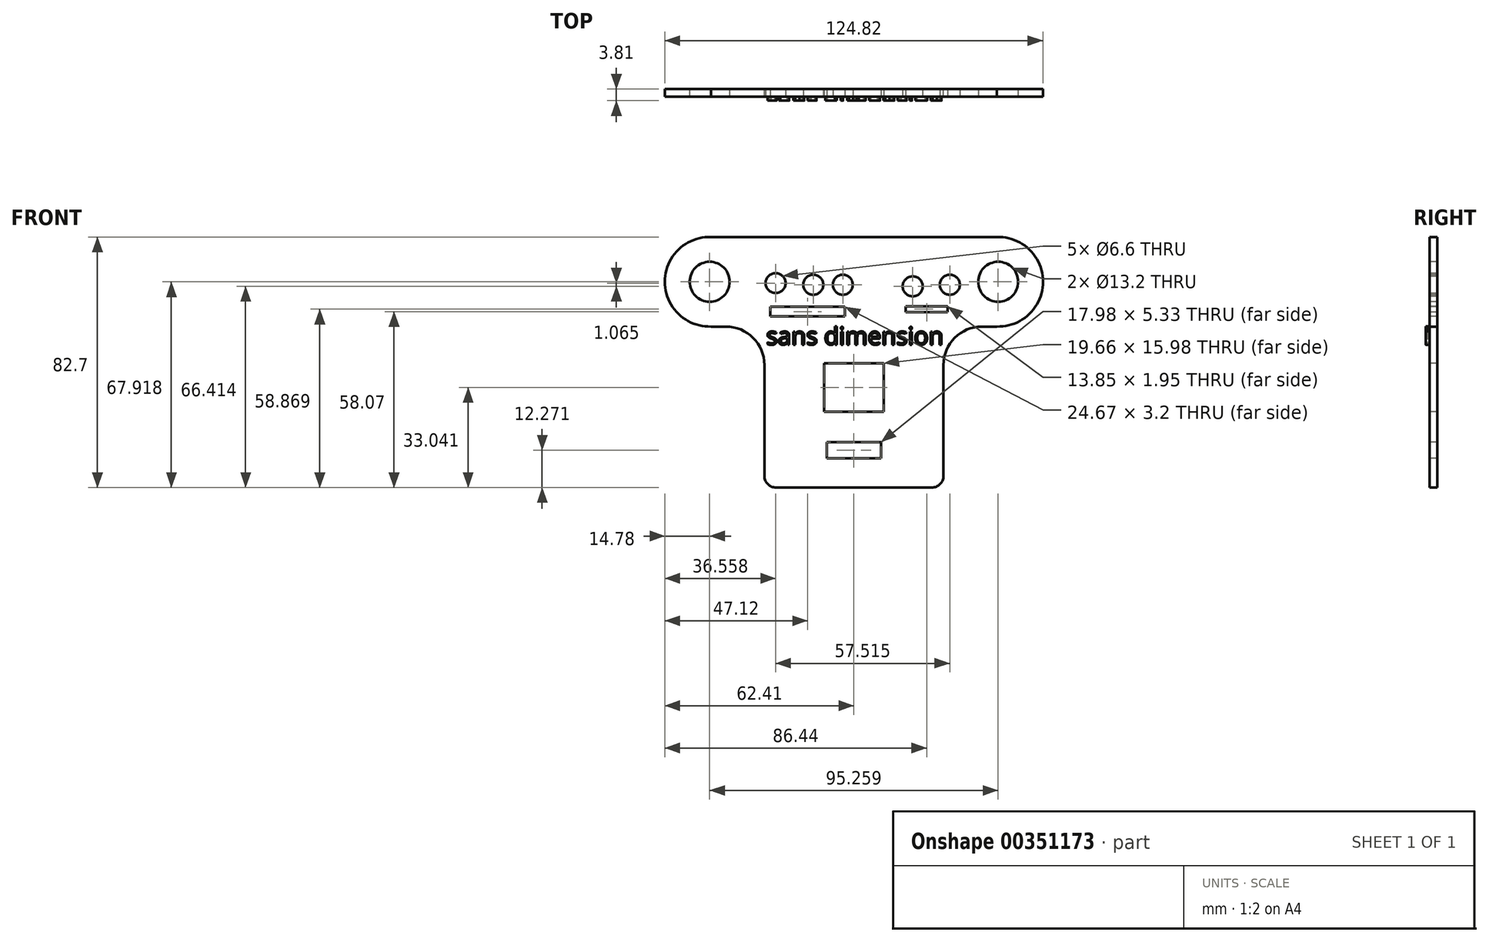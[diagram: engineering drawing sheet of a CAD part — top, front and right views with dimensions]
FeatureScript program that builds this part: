
annotation { "Feature Type Name" : "Feature", "Feature Type Description" : "" }
export const myFeature = defineFeature(function(context is Context, id is Id, definition is map)
    precondition{}
    {
        {
            var Q0;
            Q0=qCreatedBy(makeId("Front.planeOp"),FACE);
            var sketch = newSketch(context, id + "F0", { "sketchPlane" : qUnion([Q0])});
            skLineSegment(sketch, "E0.left", {"start": v(29.56, -26.57) * mm, "end": v(29.56, 26.57) * mm});
            skPoint(sketch, "E0.middle", {"position": v(0, 0) * mm});
            skLineSegment(sketch, "E1.bottom", {"start": v(47.17, 26.57) * mm, "end": v(29.56, 26.57) * mm});
            skLineSegment(sketch, "E1.top", {"start": v(47.17, 56.13) * mm, "end": v(0, 56.13) * mm});
            skArc(sketch, "E2", {"start": v(47.17, 26.57) * mm, "mid": v(62.41, 41.35) * mm, "end": v(47.17, 56.13) * mm});
            skPoint(sketch, "E2.third.point", {"position": v(62.4, 40.6) * mm});
            skPoint(sketch, "E0.right.end.orphan", {"position": v(-29.56, 26.57) * mm});
            skPoint(sketch, "E0.bottom.end.orphan", {"position": v(-29.56, -26.57) * mm});
            skLineSegment(sketch, "E3", {"start": v(0, 56.13) * mm, "end": v(0, -26.57) * mm});
            skLineSegment(sketch, "E4", {"start": v(29.56, -26.57) * mm, "end": v(0, -26.57) * mm});
            skSolve(sketch);
        }
        {
            var Q0;
            Q0 = qSketchRegion(id + "F0", true);
            extrude(context, id + "F1", {"entities" : qUnion([Q0]), "depth" : 2.54 * mm});
        }
        {
            var Q0;
            Q0=makeQuery(id+"F1.opExtrude","SWEPT_EDGE",EDGE,{"disambiguationData":[OSD([sQuery(id+"F0.wireOp",EDGE,"E0.left"),sQuery(id+"F0.wireOp",EDGE,"E1.bottom")])]});
            fillet(context, id + "F2", {"entities" : qUnion([Q0]), "radius" : 12.7 * mm, "tangentPropagation" : true, "allowEdgeOverflow" : false});
        }
        {
            var Q0;
            Q0=makeQuery(id+"F1.opExtrude","SWEPT_EDGE",EDGE,{"disambiguationData":[OSD([sQuery(id+"F0.wireOp",EDGE,"E0.left"),sQuery(id+"F0.wireOp",EDGE,"E4")])]});
            fillet(context, id + "F3", {"entities" : qUnion([Q0]), "radius" : 3.8 * mm, "tangentPropagation" : true, "allowEdgeOverflow" : false});
        }
        {
            var Q0;
            Q0=makeQuery(id+"F1.opExtrude","SWEPT_BODY",BODY,{"disambiguationData":[OSD([sQuery(id+"F0.wireOp",EDGE,"E0.left"),sQuery(id+"F0.wireOp",EDGE,"E1.bottom"),sQuery(id+"F0.wireOp",EDGE,"E1.top"),sQuery(id+"F0.wireOp",EDGE,"E2"),sQuery(id+"F0.wireOp",EDGE,"E3"),sQuery(id+"F0.wireOp",EDGE,"E4")])]});
            var Q1;
            Q1=makeQuery(id+"F1.opExtrude","SWEPT_FACE",FACE,{"disambiguationData":[OSD([sQuery(id+"F0.wireOp",EDGE,"E3")])]});
            mirror(context, id + "F4", {"operationType" : NewBodyOperationType.ADD, "entities" : qUnion([Q0]), "mirrorPlane" : qUnion([Q1])});
        }
        {
            var Q0;
            {var subQ0=makeQuery(id+"F1.opExtrude","CAP_FACE",FACE,{"disambiguationData":[OSD([sQuery(id+"F0.wireOp",EDGE,"E0.left"),sQuery(id+"F0.wireOp",EDGE,"E1.bottom"),sQuery(id+"F0.wireOp",EDGE,"E1.top"),sQuery(id+"F0.wireOp",EDGE,"E2"),sQuery(id+"F0.wireOp",EDGE,"E3"),sQuery(id+"F0.wireOp",EDGE,"E4")])],"isStart":false});Q0=makeQuery(id+"F4.boolean.opBoolean","MERGE",FACE,{"derivedFrom":[subQ0,makeQuery(id+"F4.opPattern","COPY",FACE,{"derivedFrom":subQ0,"instanceName":"1"})]});}
            var sketch = newSketch(context, id + "F5", { "sketchPlane" : qUnion([Q0])});
            skPoint(sketch, "E5", {"position": v(-47.63, 41.35) * mm});
            skPoint(sketch, "E6", {"position": v(47.63, 41.35) * mm});
            skSolve(sketch);
        }
        {
            var Q0;
            Q0=sQuery(id+"F5.wireOp",VERTEX,"E5");
            var Q1;
            Q1=sQuery(id+"F5.wireOp",VERTEX,"E6");
            var Q2;
            Q2=makeQuery(id+"F1.opExtrude","SWEPT_BODY",BODY,{"disambiguationData":[OSD([sQuery(id+"F0.wireOp",EDGE,"E0.left"),sQuery(id+"F0.wireOp",EDGE,"E1.bottom"),sQuery(id+"F0.wireOp",EDGE,"E1.top"),sQuery(id+"F0.wireOp",EDGE,"E2"),sQuery(id+"F0.wireOp",EDGE,"E3"),sQuery(id+"F0.wireOp",EDGE,"E4")])]});
            hole(context, id + "F6", {"style" : HoleStyle.SIMPLE, "endStyle" : HoleEndStyle.THROUGH, "standardTappedOrClearance" : lookupTablePath({ "standard" : "ISO", "fit" : "Normal", "size" : "M12", "type" : "Clearance" }), "standardBlindInLast" : lookupTablePath({ "fit" : "Standard", "standard" : "ISO", "size" : "M12", "type" : "Clearance" }), "holeDiameter" : 13.2 * mm, "isTappedThrough" : true, "tappedDepth" : 12.7 * mm, "tapClearance" : 3, "locations" : qUnion([Q0, Q1]), "scope" : qUnion([Q2])});
        }
        {
            var Q0;
            {var subQ0=makeQuery(id+"F1.opExtrude","CAP_FACE",FACE,{"disambiguationData":[OSD([sQuery(id+"F0.wireOp",EDGE,"E0.left"),sQuery(id+"F0.wireOp",EDGE,"E1.bottom"),sQuery(id+"F0.wireOp",EDGE,"E1.top"),sQuery(id+"F0.wireOp",EDGE,"E2"),sQuery(id+"F0.wireOp",EDGE,"E3"),sQuery(id+"F0.wireOp",EDGE,"E4")])],"isStart":false});Q0=makeQuery(id+"F4.boolean.opBoolean","MERGE",FACE,{"derivedFrom":[subQ0,makeQuery(id+"F4.opPattern","COPY",FACE,{"derivedFrom":subQ0,"instanceName":"1"})]});}
            var sketch = newSketch(context, id + "F7", { "sketchPlane" : qUnion([Q0])});
            skLineSegment(sketch, "E7.bottom", {"start": v(9.83, -1.52) * mm, "end": v(-9.83, -1.52) * mm});
            skLineSegment(sketch, "E7.top", {"start": v(9.83, 14.46) * mm, "end": v(-9.83, 14.46) * mm});
            skLineSegment(sketch, "E7.left", {"start": v(9.83, -1.52) * mm, "end": v(9.83, 14.46) * mm});
            skLineSegment(sketch, "E7.right", {"start": v(-9.83, -1.52) * mm, "end": v(-9.83, 14.46) * mm});
            skPoint(sketch, "E7.middle", {"position": v(0, 6.47) * mm});
            skLineSegment(sketch, "E8.bottom", {"start": v(-8.99, -16.96) * mm, "end": v(8.99, -16.96) * mm});
            skLineSegment(sketch, "E8.top", {"start": v(-8.99, -11.64) * mm, "end": v(8.99, -11.64) * mm});
            skLineSegment(sketch, "E8.left", {"start": v(-8.99, -16.96) * mm, "end": v(-8.99, -11.64) * mm});
            skLineSegment(sketch, "E8.right", {"start": v(8.99, -16.96) * mm, "end": v(8.99, -11.64) * mm});
            skPoint(sketch, "E8.middle", {"position": v(0, -14.3) * mm});
            skSolve(sketch);
        }
        {
            var Q0;
            Q0 = qSketchRegion(id + "F7", true);
            extrude(context, id + "F8", {"entities" : qUnion([Q0]), "operationType" : NewBodyOperationType.REMOVE, "endBound" : BoundingType.THROUGH_ALL, "oppositeDirection" : true, "depth" : 25.4 * mm});
        }
        {
            var Q0;
            {var subQ0=makeQuery(id+"F1.opExtrude","CAP_FACE",FACE,{"disambiguationData":[OSD([sQuery(id+"F0.wireOp",EDGE,"E0.left"),sQuery(id+"F0.wireOp",EDGE,"E1.bottom"),sQuery(id+"F0.wireOp",EDGE,"E1.top"),sQuery(id+"F0.wireOp",EDGE,"E2"),sQuery(id+"F0.wireOp",EDGE,"E3"),sQuery(id+"F0.wireOp",EDGE,"E4")])],"isStart":false});Q0=makeQuery(id+"F4.boolean.opBoolean","MERGE",FACE,{"derivedFrom":[subQ0,makeQuery(id+"F4.opPattern","COPY",FACE,{"derivedFrom":subQ0,"instanceName":"1"})]});}
            var sketch = newSketch(context, id + "F9", { "sketchPlane" : qUnion([Q0])});
            skPoint(sketch, "E9", {"position": v(-25.85, 40.9) * mm});
            skPoint(sketch, "E10", {"position": v(-13.43, 40.38) * mm});
            skPoint(sketch, "E11", {"position": v(-3.66, 40.38) * mm});
            skPoint(sketch, "E12", {"position": v(31.66, 40.38) * mm});
            skPoint(sketch, "E13", {"position": v(19.41, 39.84) * mm});
            skSolve(sketch);
        }
        {
            var Q0;
            Q0=sQuery(id+"F9.wireOp",VERTEX,"E9");
            var Q1;
            Q1=sQuery(id+"F9.wireOp",VERTEX,"E10");
            var Q2;
            Q2=sQuery(id+"F9.wireOp",VERTEX,"E11");
            var Q3;
            Q3=sQuery(id+"F9.wireOp",VERTEX,"E13");
            var Q4;
            Q4=sQuery(id+"F9.wireOp",VERTEX,"E12");
            var Q5;
            Q5=makeQuery(id+"F1.opExtrude","SWEPT_BODY",BODY,{"disambiguationData":[OSD([sQuery(id+"F0.wireOp",EDGE,"E0.left"),sQuery(id+"F0.wireOp",EDGE,"E1.bottom"),sQuery(id+"F0.wireOp",EDGE,"E1.top"),sQuery(id+"F0.wireOp",EDGE,"E2"),sQuery(id+"F0.wireOp",EDGE,"E3"),sQuery(id+"F0.wireOp",EDGE,"E4")])]});
            hole(context, id + "F10", {"style" : HoleStyle.SIMPLE, "endStyle" : HoleEndStyle.THROUGH, "standardTappedOrClearance" : lookupTablePath({ "standard" : "ISO", "fit" : "Normal", "size" : "M6", "type" : "Clearance" }), "standardBlindInLast" : lookupTablePath({ "fit" : "Standard", "standard" : "ISO", "size" : "M6", "type" : "Clearance" }), "holeDiameter" : 6.6 * mm, "isTappedThrough" : true, "tappedDepth" : 12.7 * mm, "tapClearance" : 3, "locations" : qUnion([Q0, Q1, Q2, Q3, Q4]), "scope" : qUnion([Q5])});
        }
        {
            var Q0;
            {var subQ0=makeQuery(id+"F1.opExtrude","CAP_FACE",FACE,{"disambiguationData":[OSD([sQuery(id+"F0.wireOp",EDGE,"E0.left"),sQuery(id+"F0.wireOp",EDGE,"E1.bottom"),sQuery(id+"F0.wireOp",EDGE,"E1.top"),sQuery(id+"F0.wireOp",EDGE,"E2"),sQuery(id+"F0.wireOp",EDGE,"E3"),sQuery(id+"F0.wireOp",EDGE,"E4")])],"isStart":false});Q0=makeQuery(id+"F4.boolean.opBoolean","MERGE",FACE,{"derivedFrom":[subQ0,makeQuery(id+"F4.opPattern","COPY",FACE,{"derivedFrom":subQ0,"instanceName":"1"})]});}
            var sketch = newSketch(context, id + "F11", { "sketchPlane" : qUnion([Q0])});
            skLineSegment(sketch, "E14.bottom", {"start": v(-27.63, 33.1) * mm, "end": v(-2.95, 33.1) * mm});
            skLineSegment(sketch, "E14.top", {"start": v(-27.63, 29.9) * mm, "end": v(-2.95, 29.9) * mm});
            skLineSegment(sketch, "E14.left", {"start": v(-27.63, 33.1) * mm, "end": v(-27.63, 29.9) * mm});
            skLineSegment(sketch, "E14.right", {"start": v(-2.95, 33.1) * mm, "end": v(-2.95, 29.9) * mm});
            skLineSegment(sketch, "E15.bottom", {"start": v(17.1, 33.28) * mm, "end": v(30.95, 33.28) * mm});
            skLineSegment(sketch, "E15.top", {"start": v(17.1, 31.32) * mm, "end": v(30.95, 31.32) * mm});
            skLineSegment(sketch, "E15.left", {"start": v(17.1, 33.28) * mm, "end": v(17.1, 31.32) * mm});
            skLineSegment(sketch, "E15.right", {"start": v(30.95, 33.28) * mm, "end": v(30.95, 31.32) * mm});
            skSolve(sketch);
        }
        {
            var Q0;
            Q0 = qSketchRegion(id + "F11", true);
            extrude(context, id + "F12", {"entities" : qUnion([Q0]), "operationType" : NewBodyOperationType.REMOVE, "oppositeDirection" : true, "depth" : 25.4 * mm});
        }
        {
            var Q0;
            {var subQ0=makeQuery(id+"F1.opExtrude","CAP_FACE",FACE,{"disambiguationData":[OSD([sQuery(id+"F0.wireOp",EDGE,"E0.left"),sQuery(id+"F0.wireOp",EDGE,"E1.bottom"),sQuery(id+"F0.wireOp",EDGE,"E1.top"),sQuery(id+"F0.wireOp",EDGE,"E2"),sQuery(id+"F0.wireOp",EDGE,"E3"),sQuery(id+"F0.wireOp",EDGE,"E4")])],"isStart":false});Q0=makeQuery(id+"F4.boolean.opBoolean","MERGE",FACE,{"derivedFrom":[subQ0,makeQuery(id+"F4.opPattern","COPY",FACE,{"derivedFrom":subQ0,"instanceName":"1"})]});}
            var sketch = newSketch(context, id + "F13", { "sketchPlane" : qUnion([Q0])});
            skText(sketch, "E16", { "text": "sans dimension\n", "fontName": "OpenSans-Regular.ttf"});
            const initialGuessF13  = {"E16": [-0.02897, 0.0206, 1, 0, 0.00577]};
            skSetInitialGuess(sketch, initialGuessF13);
            skSolve(sketch);
        }
        {
            var Q0;
            Q0 = qSketchRegion(id + "F13", true);
            extrude(context, id + "F14", {"entities" : qUnion([Q0]), "operationType" : NewBodyOperationType.ADD, "depth" : 1.27 * mm});
        }
    });
